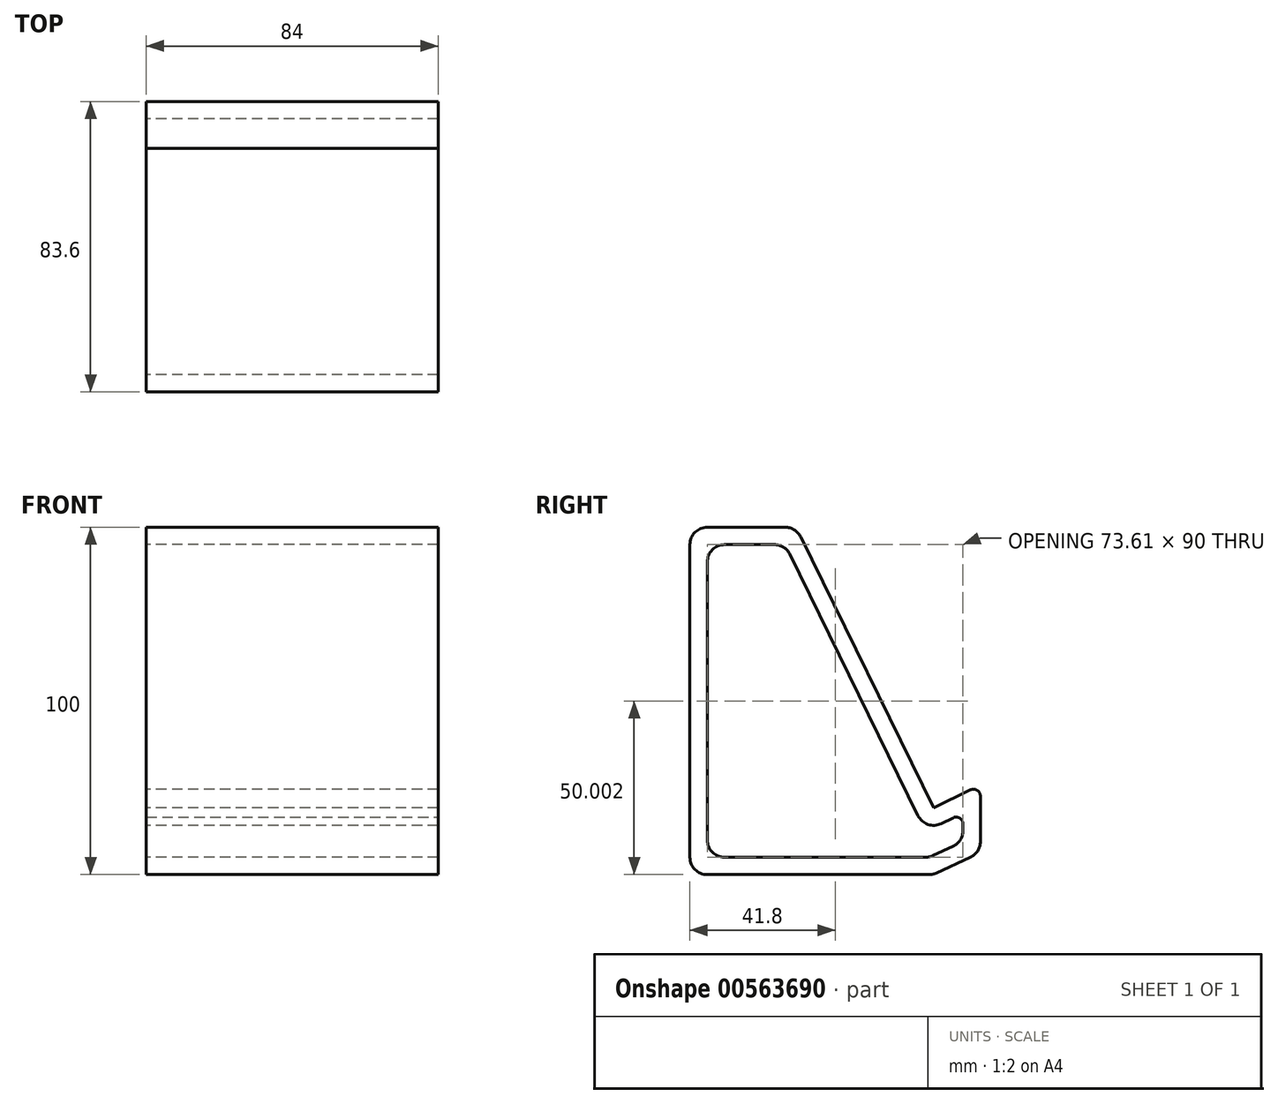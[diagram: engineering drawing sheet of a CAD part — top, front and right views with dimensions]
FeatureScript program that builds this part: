
annotation { "Feature Type Name" : "Feature", "Feature Type Description" : "" }
export const myFeature = defineFeature(function(context is Context, id is Id, definition is map)
    precondition{}
    {
        {
            var Q0;
            Q0=qCreatedBy(makeId("Right.planeOp"),FACE);
            var sketch = newSketch(context, id + "F0", { "sketchPlane" : qUnion([Q0])});
            skLineSegment(sketch, "E0", {"start": v(-61.44, 68.12) * mm, "end": v(-30.92, 68.12) * mm});
            skLineSegment(sketch, "E1", {"start": v(-30.92, 68.12) * mm, "end": v(8.7, -12.69) * mm});
            skLineSegment(sketch, "E2", {"start": v(8.7, -12.69) * mm, "end": v(22.16, -6.09) * mm});
            skLineSegment(sketch, "E3", {"start": v(22.16, -6.09) * mm, "end": v(22.16, -25.57) * mm});
            skLineSegment(sketch, "E4", {"start": v(-61.44, 68.12) * mm, "end": v(-61.44, -31.88) * mm});
            skLineSegment(sketch, "E5", {"start": v(-61.44, -31.88) * mm, "end": v(8.56, -31.88) * mm});
            skLineSegment(sketch, "E6", {"start": v(22.16, -25.57) * mm, "end": v(8.56, -31.88) * mm});
            skSolve(sketch);
        }
        {
            var Q0;
            Q0 = qSketchRegion(id + "F0", true);
            extrude(context, id + "F1", {"entities" : qUnion([Q0]), "endBound" : BoundingType.SYMMETRIC, "depth" : 84 * mm, "offsetDistance" : 25 * mm});
        }
        {
            var Q0;
            Q0=makeQuery(id+"F1.opExtrude","CAP_FACE",FACE,{"disambiguationData":[OSD([sQuery(id+"F0.wireOp",EDGE,"E0"),sQuery(id+"F0.wireOp",EDGE,"E1"),sQuery(id+"F0.wireOp",EDGE,"E2"),sQuery(id+"F0.wireOp",EDGE,"E3"),sQuery(id+"F0.wireOp",EDGE,"E4"),sQuery(id+"F0.wireOp",EDGE,"E5"),sQuery(id+"F0.wireOp",EDGE,"E6")])],"isStart":true});
            var Q1;
            Q1=makeQuery(id+"F1.opExtrude","CAP_FACE",FACE,{"disambiguationData":[OSD([sQuery(id+"F0.wireOp",EDGE,"E0"),sQuery(id+"F0.wireOp",EDGE,"E1"),sQuery(id+"F0.wireOp",EDGE,"E2"),sQuery(id+"F0.wireOp",EDGE,"E3"),sQuery(id+"F0.wireOp",EDGE,"E4"),sQuery(id+"F0.wireOp",EDGE,"E5"),sQuery(id+"F0.wireOp",EDGE,"E6")])],"isStart":false});
            shell(context, id + "F2", {"entities" : qUnion([Q0, Q1]), "thickness" : 5 * mm});
        }
        {
            var Q0;
            Q0=makeQuery(id+"F1.opExtrude","SWEPT_EDGE",EDGE,{"disambiguationData":[OSD([sQuery(id+"F0.wireOp",EDGE,"E2"),sQuery(id+"F0.wireOp",EDGE,"E3")])]});
            fillet(context, id + "F3", {"entities" : qUnion([Q0]), "radius" : 2 * mm, "tangentPropagation" : true, "allowEdgeOverflow" : false});
        }
        {
            var Q0;
            Q0=makeQuery(id+"F1.opExtrude","SWEPT_EDGE",EDGE,{"disambiguationData":[OSD([sQuery(id+"F0.wireOp",EDGE,"E3"),sQuery(id+"F0.wireOp",EDGE,"E6")])]});
            var Q1;
            Q1=makeQuery(id+"F1.opExtrude","SWEPT_EDGE",EDGE,{"disambiguationData":[OSD([sQuery(id+"F0.wireOp",EDGE,"E5"),sQuery(id+"F0.wireOp",EDGE,"E6")])]});
            var Q2;
            Q2=makeQuery(id+"F1.opExtrude","SWEPT_EDGE",EDGE,{"disambiguationData":[OSD([sQuery(id+"F0.wireOp",EDGE,"E4"),sQuery(id+"F0.wireOp",EDGE,"E5")])]});
            var Q3;
            Q3=makeQuery(id+"F1.opExtrude","SWEPT_EDGE",EDGE,{"disambiguationData":[OSD([sQuery(id+"F0.wireOp",EDGE,"E0"),sQuery(id+"F0.wireOp",EDGE,"E4")])]});
            var Q4;
            Q4=makeQuery(id+"F1.opExtrude","SWEPT_EDGE",EDGE,{"disambiguationData":[OSD([sQuery(id+"F0.wireOp",EDGE,"E0"),sQuery(id+"F0.wireOp",EDGE,"E1")])]});
            var Q5;
            Q5=makeQuery(id+"F2.opShell","OFFSET_EDGE",EDGE,{"disambiguationData":[OSD([sQuery(id+"F0.wireOp",EDGE,"E0"),sQuery(id+"F0.wireOp",EDGE,"E4")])]});
            var Q6;
            Q6=makeQuery(id+"F2.opShell","OFFSET_EDGE",EDGE,{"disambiguationData":[OSD([sQuery(id+"F0.wireOp",EDGE,"E0"),sQuery(id+"F0.wireOp",EDGE,"E1")])]});
            var Q7;
            Q7=makeQuery(id+"F2.opShell","OFFSET_EDGE",EDGE,{"disambiguationData":[OSD([sQuery(id+"F0.wireOp",EDGE,"E4"),sQuery(id+"F0.wireOp",EDGE,"E5")])]});
            var Q8;
            Q8=makeQuery(id+"F2.opShell","OFFSET_EDGE",EDGE,{"disambiguationData":[OSD([sQuery(id+"F0.wireOp",EDGE,"E3"),sQuery(id+"F0.wireOp",EDGE,"E6")])]});
            var Q9;
            Q9=makeQuery(id+"F2.opShell","OFFSET_EDGE",EDGE,{"disambiguationData":[OSD([sQuery(id+"F0.wireOp",EDGE,"E5"),sQuery(id+"F0.wireOp",EDGE,"E6")])]});
            var Q10;
            Q10=makeQuery(id+"F2.opShell","OFFSET_EDGE",EDGE,{"disambiguationData":[OSD([sQuery(id+"F0.wireOp",EDGE,"E1"),sQuery(id+"F0.wireOp",EDGE,"E2")])]});
            fillet(context, id + "F4", {"entities" : qUnion([Q0, Q1, Q2, Q3, Q4, Q5, Q6, Q7, Q8, Q9, Q10]), "radius" : 5 * mm, "tangentPropagation" : true, "allowEdgeOverflow" : false});
        }
        {
            var Q0;
            Q0=makeQuery(id+"F2.opShell","OFFSET_EDGE",EDGE,{"disambiguationData":[OSD([sQuery(id+"F0.wireOp",EDGE,"E2"),sQuery(id+"F0.wireOp",EDGE,"E3")])]});
            fillet(context, id + "F5", {"entities" : qUnion([Q0]), "radius" : 2 * mm, "tangentPropagation" : true, "allowEdgeOverflow" : false});
        }
    });
